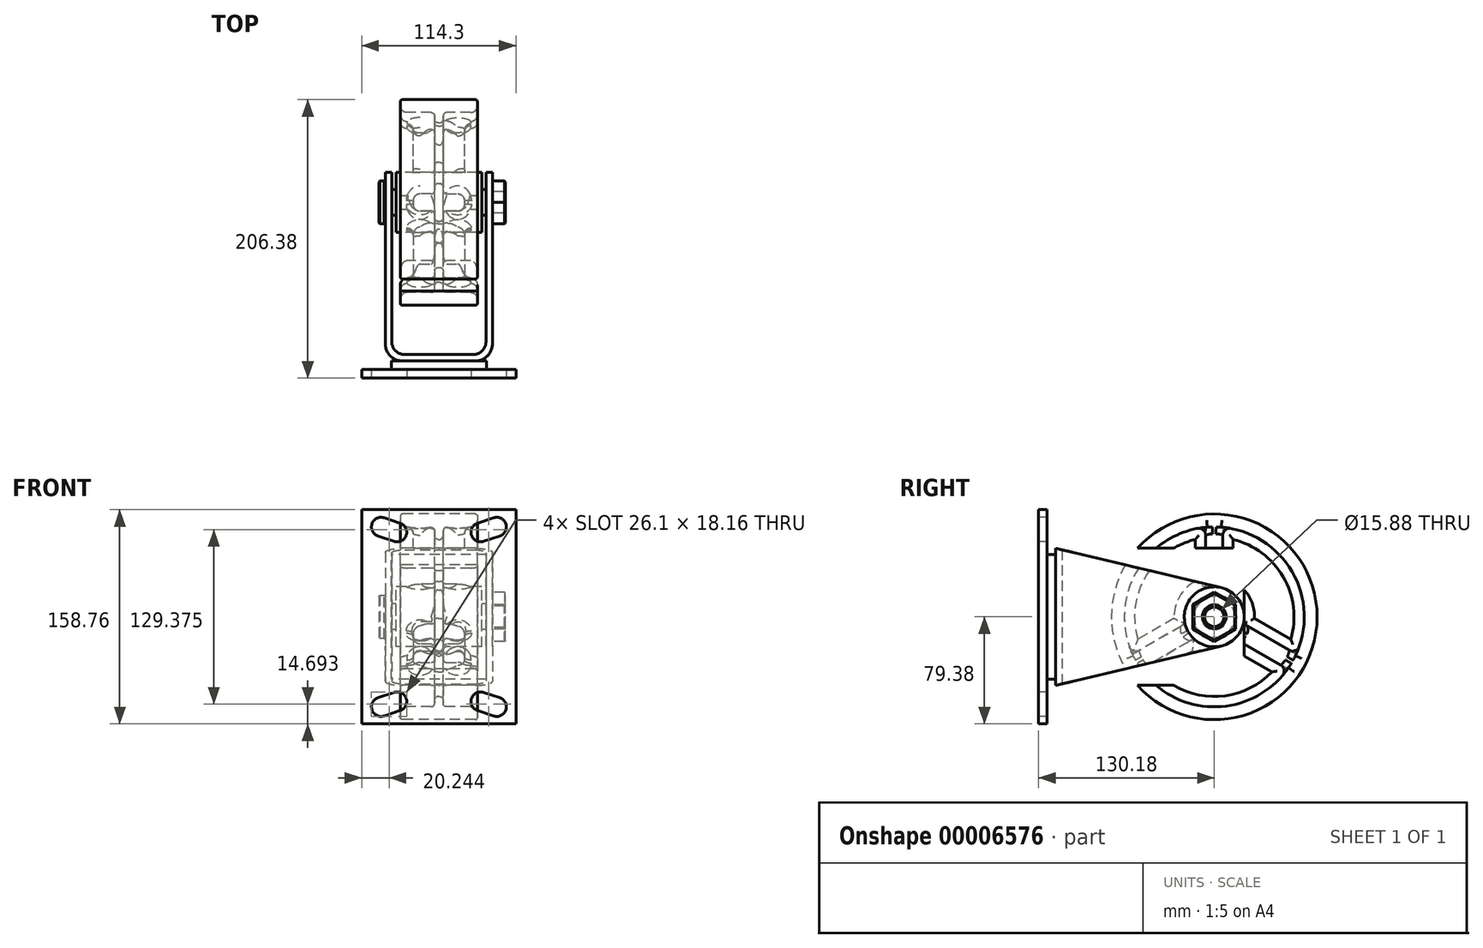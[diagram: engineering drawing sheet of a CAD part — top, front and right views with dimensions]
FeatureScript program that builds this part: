
annotation { "Feature Type Name" : "Feature", "Feature Type Description" : "" }
export const myFeature = defineFeature(function(context is Context, id is Id, definition is map)
    precondition{}
    {
        {
            var Q0;
            Q0=qCreatedBy(makeId("Right.planeOp"),FACE);
            var sketch = newSketch(context, id + "F0", { "sketchPlane" : qUnion([Q0])});
            skCircle(sketch, "E0", {"center": v(0, 0) * mm, "radius": 76.2 * mm});
            skCircle(sketch, "E1", {"center": v(0, 0) * mm, "radius": 9.53 * mm});
            skCircle(sketch, "E2.0", {"center": v(0, 0) * mm, "radius": 66.67 * mm});
            skCircle(sketch, "E3.0", {"center": v(0, 0) * mm, "radius": 22.23 * mm});
            skSolve(sketch);
        }
        {
            var Q0;
            Q0 = qSketchRegion(id + "F0", true);
            extrude(context, id + "F1", {"entities" : qUnion([Q0]), "endBound" : BoundingType.SYMMETRIC, "depth" : 57.15 * mm});
        }
        {
            var Q0;
            Q0=makeQuery(id+"F0.imprint","IMPRINT",FACE,{"disambiguationData":[TD([[makeQuery(id+"F0.imprint","IMPRINT",EDGE,{"derivedFrom":sQuery(id+"F0.wireOp",EDGE,"E2.0")}),1.0]])]});
            var Q1;
            Q1=makeQuery(id+"F0.imprint","IMPRINT",FACE,{"disambiguationData":[TD([[makeQuery(id+"F0.imprint","IMPRINT",EDGE,{"derivedFrom":sQuery(id+"F0.wireOp",EDGE,"E1")}),-1.0]])]});
            extrude(context, id + "F2", {"entities" : qUnion([Q0, Q1]), "operationType" : NewBodyOperationType.ADD, "endBound" : BoundingType.SYMMETRIC, "depth" : 6.35 * mm});
        }
        {
            var Q0;
            Q0=qCreatedBy(makeId("Right.planeOp"),FACE);
            var sketch = newSketch(context, id + "F3", { "sketchPlane" : qUnion([Q0])});
            skCircle(sketch, "E4.0", {"center": v(0, 0) * mm, "radius": 22.23 * mm});
            skCircle(sketch, "E5.0", {"center": v(0, 0) * mm, "radius": 9.53 * mm});
            skSolve(sketch);
        }
        {
            var Q0;
            Q0 = qSketchRegion(id + "F3", true);
            extrude(context, id + "F4", {"entities" : qUnion([Q0]), "operationType" : NewBodyOperationType.ADD, "endBound" : BoundingType.SYMMETRIC, "depth" : 63.5 * mm});
        }
        {
            var Q0;
            Q0=qCreatedBy(makeId("Right.planeOp"),FACE);
            var sketch = newSketch(context, id + "F5", { "sketchPlane" : qUnion([Q0])});
            skArc(sketch, "E6.0", {"start": v(-60.65, -27.69) * mm, "mid": v(-57.74, -33.34) * mm, "end": v(-54.3, -38.69) * mm});
            skArc(sketch, "E7.0", {"start": v(15.27, -16.15) * mm, "mid": v(19.25, -11.11) * mm, "end": v(21.62, -5.15) * mm});
            skLineSegment(sketch, "E8", {"start": v(0, 0) * mm, "end": v(0, 89.96) * mm, "construction": true});
            skLineSegment(sketch, "E9.0", {"start": v(-6.35, 21.3) * mm, "end": v(-6.35, 66.37) * mm});
            skLineSegment(sketch, "E10.0.MirrorCS", {"start": v(6.35, 21.3) * mm, "end": v(6.35, 66.37) * mm});
            skLineSegment(sketch, "E11.1.0", {"start": v(-15.27, -16.15) * mm, "end": v(-54.3, -38.69) * mm});
            skLineSegment(sketch, "E11.1.1", {"start": v(-21.62, -5.15) * mm, "end": v(-60.65, -27.69) * mm});
            skLineSegment(sketch, "E11.2.0", {"start": v(21.62, -5.15) * mm, "end": v(60.65, -27.69) * mm});
            skLineSegment(sketch, "E11.2.1", {"start": v(15.27, -16.15) * mm, "end": v(54.3, -38.69) * mm});
            skArc(sketch, "E12.trimOffspring", {"start": v(6.35, 66.37) * mm, "mid": v(0, 66.67) * mm, "end": v(-6.35, 66.37) * mm});
            skArc(sketch, "E13.trimOffspring", {"start": v(54.3, -38.69) * mm, "mid": v(57.74, -33.34) * mm, "end": v(60.65, -27.69) * mm});
            skArc(sketch, "E14.trimOffspring", {"start": v(-21.62, -5.15) * mm, "mid": v(-19.25, -11.11) * mm, "end": v(-15.27, -16.15) * mm});
            skArc(sketch, "E15.trimOffspring", {"start": v(6.35, 21.3) * mm, "mid": v(0, 22.22) * mm, "end": v(-6.35, 21.3) * mm});
            skSolve(sketch);
        }
        {
            var Q0;
            Q0 = qSketchRegion(id + "F5", true);
            extrude(context, id + "F6", {"entities" : qUnion([Q0]), "operationType" : NewBodyOperationType.ADD, "endBound" : BoundingType.SYMMETRIC, "depth" : 38.1 * mm});
        }
        {
            var Q0;
            {var subQ0=sQuery(id+"F0.wireOp",EDGE,"E2.0");Q0=makeQuery(id+"F6.boolean.opBoolean","SPLIT",FACE,{"disambiguationData":[TD([makeQuery(id+"F6.opExtrude","SWEPT_FACE",FACE,{"disambiguationData":[OSD([sQuery(id+"F5.wireOp",EDGE,"E11.1.0")])]})])],"derivedFrom":makeQuery(id+"F2.opExtrude","CAP_FACE",FACE,{"disambiguationData":[OSD([sQuery(id+"F0.wireOp",EDGE,"E1"),subQ0])],"isStart":false})});}
            var sketch = newSketch(context, id + "F7", { "sketchPlane" : qUnion([Q0])});
            skArc(sketch, "E16.0", {"start": v(-15.86, -25.29) * mm, "mid": v(0, -29.85) * mm, "end": v(15.86, -25.29) * mm});
            skLineSegment(sketch, "E17.0", {"start": v(-15.86, -25.29) * mm, "end": v(-42.7, -40.79) * mm});
            skArc(sketch, "E18.0", {"start": v(-42.7, -40.79) * mm, "mid": v(0, -59.05) * mm, "end": v(42.7, -40.79) * mm});
            skLineSegment(sketch, "E19.0", {"start": v(15.86, -25.29) * mm, "end": v(42.7, -40.79) * mm});
            skArc(sketch, "E20.1.0", {"start": v(29.83, -1.09) * mm, "mid": v(25.85, 14.92) * mm, "end": v(13.97, 26.37) * mm});
            skLineSegment(sketch, "E20.1.1", {"start": v(13.97, 26.37) * mm, "end": v(13.97, 57.38) * mm});
            skArc(sketch, "E20.1.2", {"start": v(56.68, -16.6) * mm, "mid": v(51.14, 29.53) * mm, "end": v(13.97, 57.38) * mm});
            skLineSegment(sketch, "E20.1.3", {"start": v(29.83, -1.09) * mm, "end": v(56.68, -16.6) * mm});
            skArc(sketch, "E20.2.0", {"start": v(-13.97, 26.37) * mm, "mid": v(-25.85, 14.92) * mm, "end": v(-29.83, -1.09) * mm});
            skLineSegment(sketch, "E20.2.1", {"start": v(-29.83, -1.09) * mm, "end": v(-56.68, -16.6) * mm});
            skArc(sketch, "E20.2.2", {"start": v(-13.97, 57.38) * mm, "mid": v(-51.14, 29.53) * mm, "end": v(-56.68, -16.6) * mm});
            skLineSegment(sketch, "E20.2.3", {"start": v(-13.97, 26.37) * mm, "end": v(-13.97, 57.38) * mm});
            skSolve(sketch);
        }
        {
            var Q0;
            Q0 = qSketchRegion(id + "F7", true);
            extrude(context, id + "F8", {"entities" : qUnion([Q0]), "operationType" : NewBodyOperationType.REMOVE, "endBound" : BoundingType.THROUGH_ALL, "oppositeDirection" : true, "depth" : 25.4 * mm});
        }
        {
            var Q0;
            {var subQ0=sQuery(id+"F0.wireOp",EDGE,"E2.0");Q0=makeQuery(id+"F6.boolean.opBoolean","SPLIT",FACE,{"disambiguationData":[TD([makeQuery(id+"F6.opExtrude","SWEPT_FACE",FACE,{"disambiguationData":[OSD([sQuery(id+"F5.wireOp",EDGE,"E10.0.MirrorCS")])]})])],"derivedFrom":makeQuery(id+"F2.opExtrude","CAP_FACE",FACE,{"disambiguationData":[OSD([sQuery(id+"F0.wireOp",EDGE,"E1"),subQ0])],"isStart":false})});}
            var Q1;
            {var subQ0=sQuery(id+"F0.wireOp",EDGE,"E2.0");Q1=makeQuery(id+"F6.boolean.opBoolean","SPLIT",FACE,{"disambiguationData":[TD([makeQuery(id+"F6.opExtrude","SWEPT_FACE",FACE,{"disambiguationData":[OSD([sQuery(id+"F5.wireOp",EDGE,"E9.0")])]})])],"derivedFrom":makeQuery(id+"F2.opExtrude","CAP_FACE",FACE,{"disambiguationData":[OSD([sQuery(id+"F0.wireOp",EDGE,"E1"),subQ0])],"isStart":false})});}
            var Q2;
            {var subQ0=sQuery(id+"F0.wireOp",EDGE,"E2.0");Q2=makeQuery(id+"F6.boolean.opBoolean","SPLIT",FACE,{"disambiguationData":[TD([makeQuery(id+"F6.opExtrude","SWEPT_FACE",FACE,{"disambiguationData":[OSD([sQuery(id+"F5.wireOp",EDGE,"E11.1.0")])]})])],"derivedFrom":makeQuery(id+"F2.opExtrude","CAP_FACE",FACE,{"disambiguationData":[OSD([sQuery(id+"F0.wireOp",EDGE,"E1"),subQ0])],"isStart":false})});}
            var Q3;
            {var subQ0=sQuery(id+"F0.wireOp",EDGE,"E2.0");Q3=makeQuery(id+"F6.boolean.opBoolean","SPLIT",FACE,{"disambiguationData":[TD([makeQuery(id+"F6.opExtrude","SWEPT_FACE",FACE,{"disambiguationData":[OSD([sQuery(id+"F5.wireOp",EDGE,"E11.1.0")])]})])],"derivedFrom":makeQuery(id+"F2.opExtrude","CAP_FACE",FACE,{"disambiguationData":[OSD([sQuery(id+"F0.wireOp",EDGE,"E1"),subQ0])],"isStart":true})});}
            var Q4;
            {var subQ0=sQuery(id+"F0.wireOp",EDGE,"E2.0");Q4=makeQuery(id+"F6.boolean.opBoolean","SPLIT",FACE,{"disambiguationData":[TD([makeQuery(id+"F6.opExtrude","SWEPT_FACE",FACE,{"disambiguationData":[OSD([sQuery(id+"F5.wireOp",EDGE,"E10.0.MirrorCS")])]})])],"derivedFrom":makeQuery(id+"F2.opExtrude","CAP_FACE",FACE,{"disambiguationData":[OSD([sQuery(id+"F0.wireOp",EDGE,"E1"),subQ0])],"isStart":true})});}
            var Q5;
            {var subQ0=sQuery(id+"F0.wireOp",EDGE,"E2.0");Q5=makeQuery(id+"F6.boolean.opBoolean","SPLIT",FACE,{"disambiguationData":[TD([makeQuery(id+"F6.opExtrude","SWEPT_FACE",FACE,{"disambiguationData":[OSD([sQuery(id+"F5.wireOp",EDGE,"E9.0")])]})])],"derivedFrom":makeQuery(id+"F2.opExtrude","CAP_FACE",FACE,{"disambiguationData":[OSD([sQuery(id+"F0.wireOp",EDGE,"E1"),subQ0])],"isStart":true})});}
            fillet(context, id + "F9", {"entities" : qUnion([Q0, Q1, Q2, Q3, Q4, Q5]), "radius" : 2.54 * mm, "tangentPropagation" : true, "allowEdgeOverflow" : false});
        }
        {
            var Q0;
            Q0=makeQuery(id+"F6.opExtrude","CAP_FACE",FACE,{"disambiguationData":[OSD([sQuery(id+"F5.wireOp",EDGE,"E9.0"),sQuery(id+"F5.wireOp",EDGE,"E10.0.MirrorCS"),sQuery(id+"F5.wireOp",EDGE,"E12.trimOffspring"),sQuery(id+"F5.wireOp",EDGE,"E15.trimOffspring")])],"isStart":true});
            var Q1;
            {var subQ0=sQuery(id+"F5.wireOp",EDGE,"E10.0.MirrorCS");var subQ1=sQuery(id+"F0.wireOp",EDGE,"E2.0");Q1=makeQuery(id+"F6.boolean.opBoolean","SPLIT",FACE,{"disambiguationData":[TD([makeQuery(id+"F2.opExtrude","CAP_FACE",FACE,{"disambiguationData":[OSD([sQuery(id+"F0.wireOp",EDGE,"E1"),subQ1])],"isStart":true})])],"derivedFrom":makeQuery(id+"F6.opExtrude","SWEPT_FACE",FACE,{"disambiguationData":[OSD([subQ0])]})});}
            var Q2;
            {var subQ0=sQuery(id+"F5.wireOp",EDGE,"E11.2.0");var subQ1=sQuery(id+"F0.wireOp",EDGE,"E2.0");Q2=makeQuery(id+"F6.boolean.opBoolean","SPLIT",FACE,{"disambiguationData":[TD([makeQuery(id+"F2.opExtrude","CAP_FACE",FACE,{"disambiguationData":[OSD([sQuery(id+"F0.wireOp",EDGE,"E1"),subQ1])],"isStart":true})])],"derivedFrom":makeQuery(id+"F6.opExtrude","SWEPT_FACE",FACE,{"disambiguationData":[OSD([subQ0])]})});}
            var Q3;
            Q3=makeQuery(id+"F6.opExtrude","CAP_FACE",FACE,{"disambiguationData":[OSD([sQuery(id+"F5.wireOp",EDGE,"E7.0"),sQuery(id+"F5.wireOp",EDGE,"E11.2.0"),sQuery(id+"F5.wireOp",EDGE,"E11.2.1"),sQuery(id+"F5.wireOp",EDGE,"E13.trimOffspring")])],"isStart":true});
            var Q4;
            Q4=makeQuery(id+"F6.opExtrude","CAP_FACE",FACE,{"disambiguationData":[OSD([sQuery(id+"F5.wireOp",EDGE,"E6.0"),sQuery(id+"F5.wireOp",EDGE,"E11.1.0"),sQuery(id+"F5.wireOp",EDGE,"E11.1.1"),sQuery(id+"F5.wireOp",EDGE,"E14.trimOffspring")])],"isStart":true});
            var Q5;
            Q5=makeQuery(id+"F6.opExtrude","CAP_FACE",FACE,{"disambiguationData":[OSD([sQuery(id+"F5.wireOp",EDGE,"E9.0"),sQuery(id+"F5.wireOp",EDGE,"E10.0.MirrorCS"),sQuery(id+"F5.wireOp",EDGE,"E12.trimOffspring"),sQuery(id+"F5.wireOp",EDGE,"E15.trimOffspring")])],"isStart":false});
            var Q6;
            Q6=makeQuery(id+"F6.opExtrude","CAP_FACE",FACE,{"disambiguationData":[OSD([sQuery(id+"F5.wireOp",EDGE,"E6.0"),sQuery(id+"F5.wireOp",EDGE,"E11.1.0"),sQuery(id+"F5.wireOp",EDGE,"E11.1.1"),sQuery(id+"F5.wireOp",EDGE,"E14.trimOffspring")])],"isStart":false});
            var Q7;
            Q7=makeQuery(id+"F6.opExtrude","CAP_FACE",FACE,{"disambiguationData":[OSD([sQuery(id+"F5.wireOp",EDGE,"E7.0"),sQuery(id+"F5.wireOp",EDGE,"E11.2.0"),sQuery(id+"F5.wireOp",EDGE,"E11.2.1"),sQuery(id+"F5.wireOp",EDGE,"E13.trimOffspring")])],"isStart":false});
            fillet(context, id + "F10", {"entities" : qUnion([Q0, Q1, Q2, Q3, Q4, Q5, Q6, Q7]), "radius" : 5.08 * mm, "tangentPropagation" : true, "allowEdgeOverflow" : false});
        }
        {
            var Q0;
            Q0=makeQuery(id+"F1.opExtrude","CAP_EDGE",EDGE,{"disambiguationData":[OSD([sQuery(id+"F0.wireOp",EDGE,"E2.0")])],"isStart":false});
            var Q1;
            Q1=makeQuery(id+"F1.opExtrude","CAP_EDGE",EDGE,{"disambiguationData":[OSD([sQuery(id+"F0.wireOp",EDGE,"E2.0")])],"isStart":true});
            fillet(context, id + "F11", {"entities" : qUnion([Q0, Q1]), "radius" : 5.08 * mm, "tangentPropagation" : true, "allowEdgeOverflow" : false});
        }
        {
            var Q0;
            Q0=makeQuery(id+"F1.opExtrude","SWEPT_FACE",FACE,{"disambiguationData":[OSD([sQuery(id+"F0.wireOp",EDGE,"E0")])]});
            fillet(context, id + "F12", {"entities" : qUnion([Q0]), "radius" : 1.52 * mm, "tangentPropagation" : true, "allowEdgeOverflow" : false});
        }
        {
            var Q0;
            Q0=qCreatedBy(makeId("Front.planeOp"),FACE);
            cPlane(context, id + "F13", {"entities" : qUnion([Q0]), "cplaneType" : CPlaneType.OFFSET, "offset" : 130.17 * mm, "width" : 152.4 * mm, "height" : 152.4 * mm});
        }
        {
            var Q0;
            Q0=qCreatedBy(id+"F13.planeOp",FACE);
            var sketch = newSketch(context, id + "F14", { "sketchPlane" : qUnion([Q0])});
            skLineSegment(sketch, "E21.rect.bottom", {"start": v(57.15, 79.38) * mm, "end": v(-57.15, 79.38) * mm});
            skLineSegment(sketch, "E21.rect.top", {"start": v(57.15, -79.38) * mm, "end": v(-57.15, -79.38) * mm});
            skLineSegment(sketch, "E21.rect.left", {"start": v(57.15, 79.38) * mm, "end": v(57.15, -79.38) * mm});
            skLineSegment(sketch, "E21.rect.right", {"start": v(-57.15, 79.38) * mm, "end": v(-57.15, -79.38) * mm});
            skPoint(sketch, "E21.rect.middle", {"position": v(0, 0) * mm});
            skLineSegment(sketch, "E22", {"start": v(57.15, 0) * mm, "end": v(-57.15, 0) * mm, "construction": true});
            skLineSegment(sketch, "E23", {"start": v(0, 79.38) * mm, "end": v(0, -79.38) * mm, "construction": true});
            skLineSegment(sketch, "E24.0", {"start": v(57.15, 66.68) * mm, "end": v(-57.15, 66.67) * mm, "construction": true});
            skLineSegment(sketch, "E25.0", {"start": v(57.15, 62.7) * mm, "end": v(-57.15, 62.7) * mm, "construction": true});
            skLineSegment(sketch, "E26.0", {"start": v(42.86, 76.2) * mm, "end": v(42.86, -76.2) * mm, "construction": true});
            skLineSegment(sketch, "E27.0", {"start": v(30.95, 76.2) * mm, "end": v(30.95, -76.2) * mm, "construction": true});
            skArc(sketch, "E28", {"start": v(28.7, 69.45) * mm, "mid": v(24.2, 60.45) * mm, "end": v(33.2, 55.95) * mm});
            skLineSegment(sketch, "E29", {"start": v(45.11, 59.93) * mm, "end": v(33.2, 55.95) * mm});
            skLineSegment(sketch, "E30", {"start": v(28.7, 69.45) * mm, "end": v(40.61, 73.42) * mm});
            skArc(sketch, "E31.trimOffspring", {"start": v(45.11, 59.93) * mm, "mid": v(49.6, 68.93) * mm, "end": v(40.61, 73.42) * mm});
            skArc(sketch, "E32.0.MirrorCS", {"start": v(45.11, -59.93) * mm, "mid": v(49.6, -68.93) * mm, "end": v(40.61, -73.42) * mm});
            skLineSegment(sketch, "E33.0.MirrorCS", {"start": v(28.7, -69.45) * mm, "end": v(40.61, -73.42) * mm});
            skLineSegment(sketch, "E34.0.MirrorCS", {"start": v(45.11, -59.93) * mm, "end": v(33.2, -55.95) * mm});
            skArc(sketch, "E35.0.MirrorCS", {"start": v(28.7, -69.45) * mm, "mid": v(24.2, -60.45) * mm, "end": v(33.2, -55.95) * mm});
            skLineSegment(sketch, "E36.0.MirrorCS", {"start": v(-45.11, -59.93) * mm, "end": v(-33.2, -55.95) * mm});
            skLineSegment(sketch, "E36.1.MirrorCS", {"start": v(-28.7, -69.45) * mm, "end": v(-40.61, -73.42) * mm});
            skLineSegment(sketch, "E36.2.MirrorCS", {"start": v(-42.86, 76.2) * mm, "end": v(-42.86, -76.2) * mm, "construction": true});
            skArc(sketch, "E36.3.MirrorCS", {"start": v(-28.7, 69.45) * mm, "mid": v(-24.2, 60.45) * mm, "end": v(-33.2, 55.95) * mm});
            skArc(sketch, "E36.4.MirrorCS", {"start": v(-45.11, -59.93) * mm, "mid": v(-49.6, -68.93) * mm, "end": v(-40.61, -73.42) * mm});
            skLineSegment(sketch, "E36.5.MirrorCS", {"start": v(-28.7, 69.45) * mm, "end": v(-40.61, 73.42) * mm});
            skArc(sketch, "E36.6.MirrorCS", {"start": v(-45.11, 59.93) * mm, "mid": v(-49.6, 68.93) * mm, "end": v(-40.61, 73.42) * mm});
            skLineSegment(sketch, "E36.7.MirrorCS", {"start": v(-30.95, 76.2) * mm, "end": v(-30.95, -76.2) * mm, "construction": true});
            skLineSegment(sketch, "E36.8.MirrorCS", {"start": v(-45.11, 59.93) * mm, "end": v(-33.2, 55.95) * mm});
            skArc(sketch, "E36.9.MirrorCS", {"start": v(-28.7, -69.45) * mm, "mid": v(-24.2, -60.45) * mm, "end": v(-33.2, -55.95) * mm});
            skSolve(sketch);
        }
        {
            var Q0;
            Q0=makeQuery(id+"F14.imprint","IMPRINT",FACE,{"disambiguationData":[TD([[makeQuery(id+"F14.imprint","IMPRINT",EDGE,{"derivedFrom":sQuery(id+"F14.wireOp",EDGE,"E21.rect.bottom")}),1.0]])]});
            extrude(context, id + "F15", {"entities" : qUnion([Q0]), "oppositeDirection" : true, "depth" : 6.38 * mm});
        }
        {
            var Q0;
            Q0=qCreatedBy(makeId("Top.planeOp"),FACE);
            var sketch = newSketch(context, id + "F16", { "sketchPlane" : qUnion([Q0])});
            skLineSegment(sketch, "E37.0", {"start": v(-34.92, 22.23) * mm, "end": v(-34.92, -112.67) * mm});
            skLineSegment(sketch, "E38.0", {"start": v(0, -117.45) * mm, "end": v(-39.7, -117.45) * mm});
            skLineSegment(sketch, "E39.0", {"start": v(0, -112.67) * mm, "end": v(-34.92, -112.67) * mm});
            skLineSegment(sketch, "E40.0", {"start": v(-39.7, 22.23) * mm, "end": v(-39.7, -117.45) * mm});
            skLineSegment(sketch, "E41", {"start": v(0, 0) * mm, "end": v(0, -149.02) * mm, "construction": true});
            skLineSegment(sketch, "E42", {"start": v(-39.7, 22.23) * mm, "end": v(-34.92, 22.23) * mm});
            skLineSegment(sketch, "E43.0.MirrorCS", {"start": v(0, -112.67) * mm, "end": v(34.92, -112.67) * mm});
            skLineSegment(sketch, "E44.0.MirrorCS", {"start": v(0, -117.45) * mm, "end": v(39.7, -117.45) * mm});
            skLineSegment(sketch, "E45.0.MirrorCS", {"start": v(34.92, 22.23) * mm, "end": v(34.92, -112.67) * mm});
            skLineSegment(sketch, "E46.0.MirrorCS", {"start": v(39.7, 22.23) * mm, "end": v(39.7, -117.45) * mm});
            skLineSegment(sketch, "E47.0.MirrorCS", {"start": v(39.7, 22.23) * mm, "end": v(34.92, 22.23) * mm});
            skSolve(sketch);
        }
        {
            var Q0;
            Q0 = qSketchRegion(id + "F16", true);
            extrude(context, id + "F17", {"entities" : qUnion([Q0]), "endBound" : BoundingType.SYMMETRIC, "depth" : 101.6 * mm});
        }
        {
            var Q0;
            Q0=makeQuery(id+"F17.opExtrude","SWEPT_FACE",FACE,{"disambiguationData":[OSD([sQuery(id+"F16.wireOp",EDGE,"E40.0")])]});
            var sketch = newSketch(context, id + "F18", { "sketchPlane" : qUnion([Q0])});
            skArc(sketch, "E48.0", {"start": v(-5.15, -21.62) * mm, "mid": v(-22.23, 0) * mm, "end": v(-5.15, 21.62) * mm});
            skLineSegment(sketch, "E49", {"start": v(117.45, 50.8) * mm, "end": v(-5.15, 21.62) * mm});
            skLineSegment(sketch, "E50", {"start": v(117.45, -50.8) * mm, "end": v(-5.15, -21.62) * mm});
            skCircle(sketch, "E51.0", {"center": v(0, 0) * mm, "radius": 9.53 * mm});
            skLineSegment(sketch, "E52.0", {"start": v(-22.23, 50.8) * mm, "end": v(117.45, 50.8) * mm});
            skLineSegment(sketch, "E53.0", {"start": v(-22.23, 50.8) * mm, "end": v(-22.23, -50.8) * mm});
            skLineSegment(sketch, "E54.0", {"start": v(-22.23, -50.8) * mm, "end": v(117.45, -50.8) * mm});
            skSolve(sketch);
        }
        {
            var Q0;
            Q0 = qSketchRegion(id + "F18", true);
            extrude(context, id + "F19", {"entities" : qUnion([Q0]), "operationType" : NewBodyOperationType.REMOVE, "oppositeDirection" : true, "depth" : 101.6 * mm});
        }
        {
            var Q0;
            Q0=makeQuery(id+"F17.opExtrude","SWEPT_EDGE",EDGE,{"disambiguationData":[OSD([sQuery(id+"F16.wireOp",EDGE,"E43.0.MirrorCS"),sQuery(id+"F16.wireOp",EDGE,"E45.0.MirrorCS")])]});
            var Q1;
            Q1=makeQuery(id+"F17.opExtrude","SWEPT_EDGE",EDGE,{"disambiguationData":[OSD([sQuery(id+"F16.wireOp",EDGE,"E37.0"),sQuery(id+"F16.wireOp",EDGE,"E39.0")])]});
            fillet(context, id + "F20", {"entities" : qUnion([Q0, Q1]), "radius" : 9.52 * mm, "tangentPropagation" : true, "allowEdgeOverflow" : false});
        }
        {
            var Q0;
            Q0=makeQuery(id+"F17.opExtrude","SWEPT_EDGE",EDGE,{"disambiguationData":[OSD([sQuery(id+"F16.wireOp",EDGE,"E44.0.MirrorCS"),sQuery(id+"F16.wireOp",EDGE,"E46.0.MirrorCS")])]});
            var Q1;
            Q1=makeQuery(id+"F17.opExtrude","SWEPT_EDGE",EDGE,{"disambiguationData":[OSD([sQuery(id+"F16.wireOp",EDGE,"E38.0"),sQuery(id+"F16.wireOp",EDGE,"E40.0")])]});
            fillet(context, id + "F21", {"entities" : qUnion([Q0, Q1]), "radius" : 12.7 * mm, "tangentPropagation" : true, "allowEdgeOverflow" : false});
        }
        {
            var Q0;
            Q0=makeQuery(id+"F17.opExtrude","SWEPT_FACE",FACE,{"disambiguationData":[OSD([sQuery(id+"F16.wireOp",EDGE,"E40.0")])]});
            var sketch = newSketch(context, id + "F22", { "sketchPlane" : qUnion([Q0])});
            skCircle(sketch, "E55", {"center": v(0, 0) * mm, "radius": 15.88 * mm});
            skSolve(sketch);
        }
        {
            var Q0;
            Q0 = qSketchRegion(id + "F22", true);
            extrude(context, id + "F23", {"entities" : qUnion([Q0]), "depth" : 4.78 * mm});
        }
        {
            var Q0;
            Q0=makeQuery(id+"F23.opExtrude","CAP_FACE",FACE,{"disambiguationData":[OSD([sQuery(id+"F22.wireOp",EDGE,"E55")])],"isStart":true});
            var sketch = newSketch(context, id + "F24", { "sketchPlane" : qUnion([Q0])});
            skCircle(sketch, "E56", {"center": v(0, 0) * mm, "radius": 9.53 * mm});
            skSolve(sketch);
        }
        {
            var Q0;
            Q0 = qSketchRegion(id + "F24", true);
            extrude(context, id + "F25", {"entities" : qUnion([Q0]), "operationType" : NewBodyOperationType.ADD, "depth" : 79.43 * mm});
        }
        {
            var Q0;
            Q0=makeQuery(id+"F25.opExtrude","CAP_FACE",FACE,{"disambiguationData":[OSD([sQuery(id+"F24.wireOp",EDGE,"E56")])],"isStart":false});
            var sketch = newSketch(context, id + "F26", { "sketchPlane" : qUnion([Q0])});
            skCircle(sketch, "E57", {"center": v(0, 0) * mm, "radius": 7.94 * mm});
            skSolve(sketch);
        }
        {
            var Q0;
            Q0 = qSketchRegion(id + "F26", true);
            extrude(context, id + "F27", {"entities" : qUnion([Q0]), "operationType" : NewBodyOperationType.ADD, "depth" : 9.52 * mm});
        }
        {
            var Q0;
            Q0=makeQuery(id+"F27.opExtrude","CAP_FACE",FACE,{"disambiguationData":[OSD([sQuery(id+"F26.wireOp",EDGE,"E57")])],"isStart":false});
            chamfer(context, id + "F28", {"entities" : qUnion([Q0]), "width" : 0.76 * mm, "tangentPropagation" : true});
        }
        {
            var Q0;
            Q0=makeQuery(id+"F25.opExtrude","CAP_FACE",FACE,{"disambiguationData":[OSD([sQuery(id+"F24.wireOp",EDGE,"E56")])],"isStart":false});
            var sketch = newSketch(context, id + "F29", { "sketchPlane" : qUnion([Q0])});
            skCircle(sketch, "E58.cCircle", {"center": v(0, 0) * mm, "radius": 15.88 * mm, "construction": true});
            skLineSegment(sketch, "E58.0", {"start": v(15.88, 9.17) * mm, "end": v(15.88, -9.17) * mm});
            skLineSegment(sketch, "E58.1", {"start": v(15.88, -9.17) * mm, "end": v(0, -18.33) * mm});
            skLineSegment(sketch, "E58.2", {"start": v(0, -18.33) * mm, "end": v(-15.88, -9.17) * mm});
            skLineSegment(sketch, "E58.3", {"start": v(-15.88, -9.17) * mm, "end": v(-15.88, 9.17) * mm});
            skLineSegment(sketch, "E58.4", {"start": v(-15.88, 9.17) * mm, "end": v(0, 18.33) * mm});
            skLineSegment(sketch, "E58.5", {"start": v(0, 18.33) * mm, "end": v(15.87, 9.17) * mm});
            skPoint(sketch, "E58.0.midPoint", {"position": v(15.88, 0) * mm});
            skCircle(sketch, "E59.0", {"center": v(0, 0) * mm, "radius": 7.94 * mm});
            skSolve(sketch);
        }
        {
            var Q0;
            Q0 = qSketchRegion(id + "F29", true);
            var Q1;
            Q1=makeQuery(id+"F27.opExtrude","CAP_FACE",FACE,{"disambiguationData":[OSD([sQuery(id+"F26.wireOp",EDGE,"E57")])],"isStart":false});
            extrude(context, id + "F30", {"entities" : qUnion([Q0]), "endBound" : BoundingType.UP_TO_SURFACE, "endBoundEntityFace" : qUnion([Q1]), "depth" : 25.4 * mm});
        }
        {
            var Q0;
            Q0=makeQuery(id+"F15.opExtrude","CAP_FACE",FACE,{"disambiguationData":[OSD([sQuery(id+"F14.wireOp",EDGE,"E21.rect.bottom"),sQuery(id+"F14.wireOp",EDGE,"E21.rect.top"),sQuery(id+"F14.wireOp",EDGE,"E21.rect.left"),sQuery(id+"F14.wireOp",EDGE,"E21.rect.right"),sQuery(id+"F14.wireOp",EDGE,"E28"),sQuery(id+"F14.wireOp",EDGE,"E29"),sQuery(id+"F14.wireOp",EDGE,"E30"),sQuery(id+"F14.wireOp",EDGE,"E31.trimOffspring"),sQuery(id+"F14.wireOp",EDGE,"E32.0.MirrorCS"),sQuery(id+"F14.wireOp",EDGE,"E33.0.MirrorCS"),sQuery(id+"F14.wireOp",EDGE,"E34.0.MirrorCS"),sQuery(id+"F14.wireOp",EDGE,"E35.0.MirrorCS"),sQuery(id+"F14.wireOp",EDGE,"E36.0.MirrorCS"),sQuery(id+"F14.wireOp",EDGE,"E36.1.MirrorCS"),sQuery(id+"F14.wireOp",EDGE,"E36.3.MirrorCS"),sQuery(id+"F14.wireOp",EDGE,"E36.4.MirrorCS"),sQuery(id+"F14.wireOp",EDGE,"E36.5.MirrorCS"),sQuery(id+"F14.wireOp",EDGE,"E36.6.MirrorCS"),sQuery(id+"F14.wireOp",EDGE,"E36.8.MirrorCS"),sQuery(id+"F14.wireOp",EDGE,"E36.9.MirrorCS")])],"isStart":false});
            var sketch = newSketch(context, id + "F31", { "sketchPlane" : qUnion([Q0])});
            skLineSegment(sketch, "E60.rect.bottom", {"start": v(-35.19, -46.09) * mm, "end": v(35.19, -46.09) * mm});
            skLineSegment(sketch, "E60.rect.top", {"start": v(-35.19, 46.09) * mm, "end": v(35.19, 46.09) * mm});
            skLineSegment(sketch, "E60.rect.left", {"start": v(-35.19, -46.09) * mm, "end": v(-35.19, 46.09) * mm});
            skLineSegment(sketch, "E60.rect.right", {"start": v(35.19, -46.09) * mm, "end": v(35.19, 46.09) * mm});
            skPoint(sketch, "E60.rect.middle", {"position": v(0, 0) * mm});
            skSolve(sketch);
        }
        {
            var Q0;
            Q0 = qSketchRegion(id + "F31", true);
            extrude(context, id + "F32", {"entities" : qUnion([Q0]), "depth" : 6.35 * mm});
        }
        {
            var Q0;
            Q0=makeQuery(id+"F30.opExtrude","CAP_FACE",FACE,{"disambiguationData":[OSD([sQuery(id+"F29.wireOp",EDGE,"E58.0"),sQuery(id+"F29.wireOp",EDGE,"E58.1"),sQuery(id+"F29.wireOp",EDGE,"E58.2"),sQuery(id+"F29.wireOp",EDGE,"E58.3"),sQuery(id+"F29.wireOp",EDGE,"E58.4"),sQuery(id+"F29.wireOp",EDGE,"E58.5"),sQuery(id+"F29.wireOp",EDGE,"E59.0")])],"isStart":false});
            chamfer(context, id + "F33", {"entities" : qUnion([Q0]), "width" : 0.76 * mm, "tangentPropagation" : true});
        }
        {
            var Q0;
            Q0=makeQuery(id+"F23.opExtrude","SWEPT_FACE",FACE,{"disambiguationData":[OSD([sQuery(id+"F22.wireOp",EDGE,"E55")])]});
            chamfer(context, id + "F34", {"entities" : qUnion([Q0]), "width" : 0.76 * mm, "tangentPropagation" : true});
        }
    });
